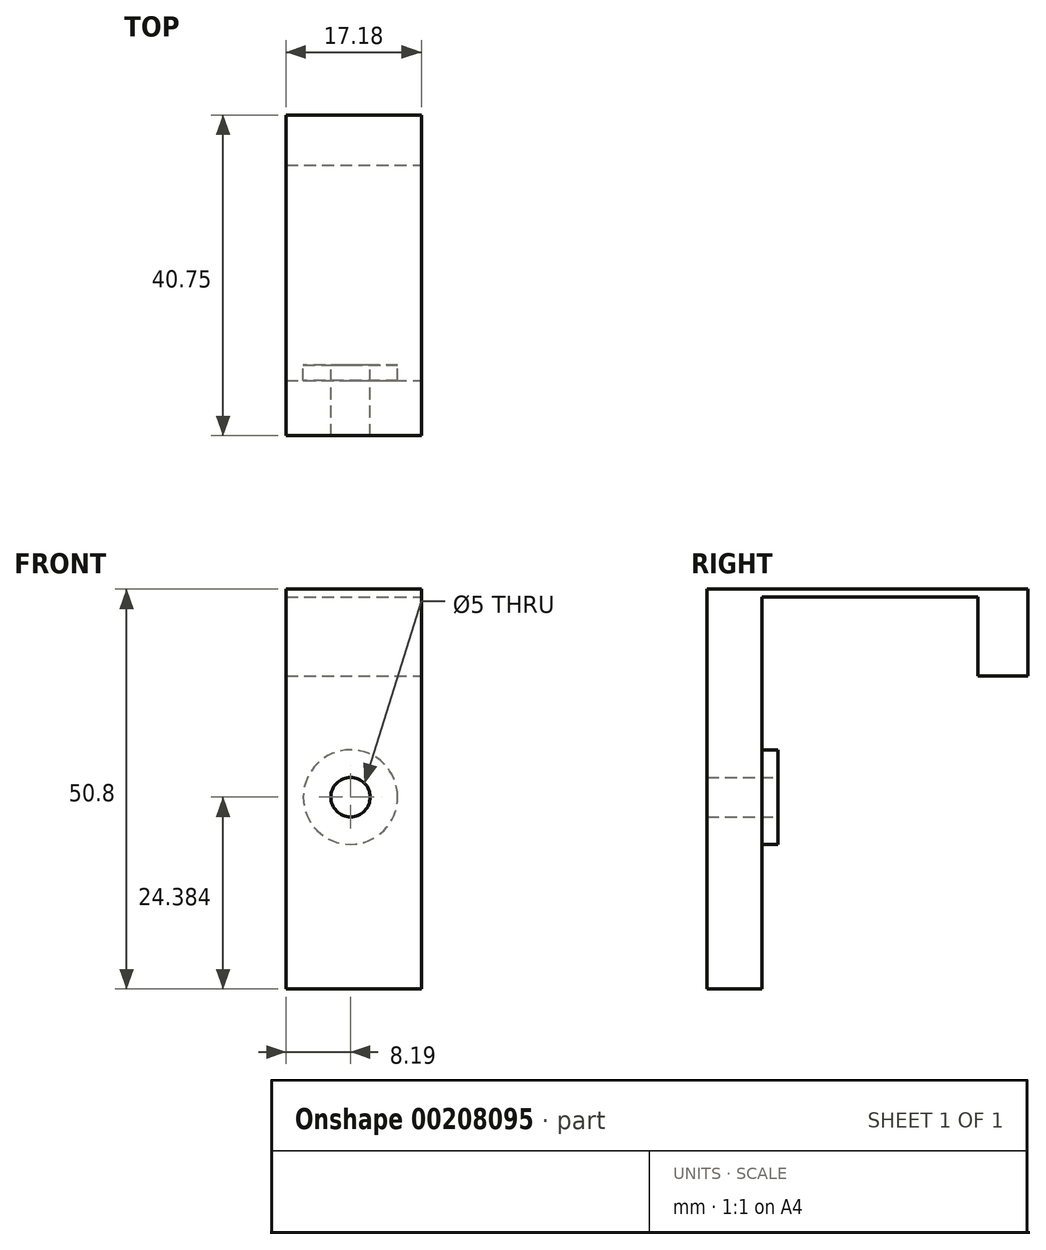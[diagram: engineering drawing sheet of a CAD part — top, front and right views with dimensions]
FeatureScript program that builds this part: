
annotation { "Feature Type Name" : "Feature", "Feature Type Description" : "" }
export const myFeature = defineFeature(function(context is Context, id is Id, definition is map)
    precondition{}
    {
        {
            var Q0;
            Q0=qCreatedBy(makeId("Front.planeOp"),FACE);
            var sketch = newSketch(context, id + "F0", { "sketchPlane" : qUnion([Q0])});
            skLineSegment(sketch, "E0.bottom", {"start": v(25.4, -38.1) * mm, "end": v(-25.4, -38.1) * mm});
            skLineSegment(sketch, "E0.top", {"start": v(25.4, 38.1) * mm, "end": v(-25.4, 38.1) * mm});
            skLineSegment(sketch, "E0.left", {"start": v(25.4, -38.1) * mm, "end": v(25.4, 38.1) * mm});
            skLineSegment(sketch, "E0.right", {"start": v(-25.4, -38.1) * mm, "end": v(-25.4, 38.1) * mm});
            skPoint(sketch, "E0.middle", {"position": v(0, 0) * mm});
            skSolve(sketch);
        }
        {
            var Q0;
            Q0=makeQuery(id+"F0.imprint","IMPRINT",FACE,{"disambiguationData":[TD([[makeQuery(id+"F0.imprint","IMPRINT",EDGE,{"derivedFrom":sQuery(id+"F0.wireOp",EDGE,"E0.bottom")}),-1.0]])]});
            extrude(context, id + "F1", {"entities" : qUnion([Q0]), "depth" : 50.8 * mm});
        }
        {
            var Q0;
            Q0=qCreatedBy(makeId("Front.planeOp"),FACE);
            var sketch = newSketch(context, id + "F2", { "sketchPlane" : qUnion([Q0])});
            skLineSegment(sketch, "E1.bottom", {"start": v(-57.9, 37.08) * mm, "end": v(60.26, 37.08) * mm});
            skLineSegment(sketch, "E1.top", {"start": v(-57.9, -47.42) * mm, "end": v(60.26, -47.42) * mm});
            skLineSegment(sketch, "E1.left", {"start": v(-57.9, 37.08) * mm, "end": v(-57.9, -47.42) * mm});
            skLineSegment(sketch, "E1.right", {"start": v(60.26, 37.08) * mm, "end": v(60.26, -47.42) * mm});
            skLineSegment(sketch, "E2.0", {"start": v(25.4, 37.1) * mm, "end": v(-25.4, 37.1) * mm});
            skSolve(sketch);
        }
        {
            var Q0;
            Q0 = qSketchRegion(id + "F2", true);
            extrude(context, id + "F3", {"entities" : qUnion([Q0]), "depth" : 25.4 * mm});
        }
        {
            var Q0;
            Q0=makeQuery(id+"F3.opExtrude","SWEPT_BODY",BODY,{"disambiguationData":[OSD([sQuery(id+"F2.wireOp",EDGE,"E1.bottom"),sQuery(id+"F2.wireOp",EDGE,"E1.top"),sQuery(id+"F2.wireOp",EDGE,"E1.left"),sQuery(id+"F2.wireOp",EDGE,"E1.right")])]});
            var Q1;
            Q1=qCreatedBy(makeId("Front.planeOp"),FACE);
            transform(context, id + "F4", {"entities" : qUnion([Q0]), "transformType" : TransformType.TRANSLATION_DISTANCE, "transformDirection" : qUnion([Q1]), "distance" : 6.35 * mm, "makeCopy" : false});
        }
        {
            var Q0;
            Q0=makeQuery(id+"F3.opExtrude","SWEPT_BODY",BODY,{"disambiguationData":[OSD([sQuery(id+"F2.wireOp",EDGE,"E1.bottom"),sQuery(id+"F2.wireOp",EDGE,"E1.top"),sQuery(id+"F2.wireOp",EDGE,"E1.left"),sQuery(id+"F2.wireOp",EDGE,"E1.right")])]});
            var Q1;
            Q1=makeQuery(id+"F1.opExtrude","SWEPT_BODY",BODY,{"disambiguationData":[OSD([sQuery(id+"F0.wireOp",EDGE,"E0.bottom"),sQuery(id+"F0.wireOp",EDGE,"E0.top"),sQuery(id+"F0.wireOp",EDGE,"E0.left"),sQuery(id+"F0.wireOp",EDGE,"E0.right")])]});
            booleanBodies(context, id + "F5", {"operationType" : BooleanOperationType.SUBTRACTION, "tools" : qUnion([Q0]), "targets" : qUnion([Q1])});
        }
        {
            var Q0;
            Q0=makeQuery(id+"F5.opBoolean","COPY",FACE,{"derivedFrom":makeQuery(id+"F3.opExtrude","CAP_FACE",FACE,{"disambiguationData":[OSD([sQuery(id+"F2.wireOp",EDGE,"E1.bottom"),sQuery(id+"F2.wireOp",EDGE,"E1.top"),sQuery(id+"F2.wireOp",EDGE,"E1.left"),sQuery(id+"F2.wireOp",EDGE,"E1.right")])],"isStart":false})});
            var sketch = newSketch(context, id + "F6", { "sketchPlane" : qUnion([Q0])});
            skSolve(sketch);
        }
        {
            var Q0;
            Q0=makeQuery(id+"F1.opExtrude","CAP_FACE",FACE,{"disambiguationData":[OSD([sQuery(id+"F0.wireOp",EDGE,"E0.bottom"),sQuery(id+"F0.wireOp",EDGE,"E0.top"),sQuery(id+"F0.wireOp",EDGE,"E0.left"),sQuery(id+"F0.wireOp",EDGE,"E0.right")])],"isStart":true});
            var sketch = newSketch(context, id + "F7", { "sketchPlane" : qUnion([Q0])});
            skLineSegment(sketch, "E3.0", {"start": v(-25.4, 27.1) * mm, "end": v(25.4, 27.1) * mm});
            skSolve(sketch);
        }
        {
            var Q0;
            {var subQ0=sQuery(id+"F7.wireOp",EDGE,"E3.0");Q0=makeQuery(id+"F7.imprint","IMPRINT",FACE,{"disambiguationData":[TD([[makeQuery(id+"F7.imprint","IMPRINT",EDGE,{"derivedFrom":subQ0}),-1.0]])]});}
            extrude(context, id + "F8", {"entities" : qUnion([Q0]), "operationType" : NewBodyOperationType.REMOVE, "oppositeDirection" : true, "depth" : 25.4 * mm});
        }
        {
            var Q0;
            {var subQ0=sQuery(id+"F2.wireOp",EDGE,"E1.bottom");Q0=makeQuery(id+"F6.imprint","IMPRINT",FACE,{"disambiguationData":[TD([[makeQuery(id+"F6.imprint","IMPRINT",EDGE,{"derivedFrom":makeQuery(id+"F5.opBoolean","COPY",EDGE,{"derivedFrom":makeQuery(id+"F3.opExtrude","CAP_EDGE",EDGE,{"disambiguationData":[OSD([subQ0])],"isStart":false})})}),1.0]])]});}
            var sketch = newSketch(context, id + "F9", { "sketchPlane" : qUnion([Q0])});
            skLineSegment(sketch, "E4.0", {"start": v(25.4, 11.68) * mm, "end": v(-25.4, 11.68) * mm});
            skCircle(sketch, "E5", {"center": v(0, 11.68) * mm, "radius": 6 * mm});
            skSolve(sketch);
        }
        {
            var Q0;
            {var subQ0=sQuery(id+"F9.wireOp",EDGE,"E5");var subQ1=sQuery(id+"F9.wireOp",EDGE,"E4.0");var subQ2=makeQuery(id+"F9.imprint","INTERSECT",VERTEX,{"disambiguationData":[OD(0.0)],"derivedFrom":[subQ1,subQ0]});Q0=makeQuery(id+"F9.imprint","IMPRINT",FACE,{"disambiguationData":[TD([[makeQuery(id+"F9.imprint","IMPRINT",EDGE,{"disambiguationData":[TD([[subQ2,-1.0]])],"derivedFrom":subQ1}),-1.0]])]});}
            var Q1;
            {var subQ0=sQuery(id+"F9.wireOp",EDGE,"E5");var subQ1=sQuery(id+"F9.wireOp",EDGE,"E4.0");var subQ2=makeQuery(id+"F9.imprint","INTERSECT",VERTEX,{"disambiguationData":[OD(0.0)],"derivedFrom":[subQ1,subQ0]});Q1=makeQuery(id+"F9.imprint","IMPRINT",FACE,{"disambiguationData":[TD([[makeQuery(id+"F9.imprint","IMPRINT",EDGE,{"disambiguationData":[TD([[subQ2,-1.0]])],"derivedFrom":subQ1}),1.0]])]});}
            extrude(context, id + "F10", {"entities" : qUnion([Q0, Q1]), "operationType" : NewBodyOperationType.REMOVE, "oppositeDirection" : true, "depth" : 2 * mm});
        }
        {
            var Q0;
            {var subQ0=sQuery(id+"F2.wireOp",EDGE,"E1.bottom");Q0=makeQuery(id+"F6.imprint","IMPRINT",FACE,{"disambiguationData":[TD([[makeQuery(id+"F6.imprint","IMPRINT",EDGE,{"derivedFrom":makeQuery(id+"F5.opBoolean","COPY",EDGE,{"derivedFrom":makeQuery(id+"F3.opExtrude","CAP_EDGE",EDGE,{"disambiguationData":[OSD([subQ0])],"isStart":false})})}),1.0]])]});}
            var sketch = newSketch(context, id + "F11", { "sketchPlane" : qUnion([Q0])});
            skCircle(sketch, "E6", {"center": v(0, 11.68) * mm, "radius": 2.5 * mm});
            skSolve(sketch);
        }
        {
            var Q0;
            Q0=makeQuery(id+"F11.imprint","IMPRINT",FACE,{"disambiguationData":[TD([[makeQuery(id+"F11.imprint","IMPRINT",EDGE,{"derivedFrom":sQuery(id+"F11.wireOp",EDGE,"E6")}),1.0]])]});
            extrude(context, id + "F12", {"entities" : qUnion([Q0]), "operationType" : NewBodyOperationType.REMOVE, "oppositeDirection" : true, "depth" : 25.4 * mm});
        }
        {
            var Q0;
            Q0=makeQuery(id+"F1.opExtrude","CAP_FACE",FACE,{"disambiguationData":[OSD([sQuery(id+"F0.wireOp",EDGE,"E0.bottom"),sQuery(id+"F0.wireOp",EDGE,"E0.top"),sQuery(id+"F0.wireOp",EDGE,"E0.left"),sQuery(id+"F0.wireOp",EDGE,"E0.right")])],"isStart":false});
            var sketch = newSketch(context, id + "F13", { "sketchPlane" : qUnion([Q0])});
            skLineSegment(sketch, "E7.0", {"start": v(25.4, -12.7) * mm, "end": v(-25.4, -12.7) * mm});
            skSolve(sketch);
        }
        {
            var Q0;
            {var subQ0=sQuery(id+"F13.wireOp",EDGE,"E7.0");Q0=makeQuery(id+"F13.imprint","IMPRINT",FACE,{"disambiguationData":[TD([[makeQuery(id+"F13.imprint","IMPRINT",EDGE,{"derivedFrom":subQ0}),1.0]])]});}
            extrude(context, id + "F14", {"entities" : qUnion([Q0]), "operationType" : NewBodyOperationType.REMOVE, "oppositeDirection" : true, "depth" : 25.4 * mm});
        }
        {
            var Q0;
            Q0=qCreatedBy(makeId("Front.planeOp"),FACE);
            var sketch = newSketch(context, id + "F15", { "sketchPlane" : qUnion([Q0])});
            skLineSegment(sketch, "E8.bottom", {"start": v(9, 38.4) * mm, "end": v(32.67, 38.4) * mm});
            skLineSegment(sketch, "E8.top", {"start": v(9, -15) * mm, "end": v(32.67, -15) * mm});
            skLineSegment(sketch, "E8.left", {"start": v(9, 38.4) * mm, "end": v(9, -15) * mm});
            skLineSegment(sketch, "E8.right", {"start": v(32.67, 38.4) * mm, "end": v(32.67, -15) * mm});
            skLineSegment(sketch, "E9.bottom", {"start": v(28.87, 38.4) * mm, "end": v(32.67, 38.4) * mm});
            skLineSegment(sketch, "E9.top", {"start": v(28.87, 38.4) * mm, "end": v(32.67, 38.4) * mm});
            skLineSegment(sketch, "E9.left", {"start": v(28.87, 38.4) * mm, "end": v(28.87, 38.4) * mm});
            skLineSegment(sketch, "E9.right", {"start": v(32.67, 38.4) * mm, "end": v(32.67, 38.4) * mm});
            skSolve(sketch);
        }
        {
            var Q0;
            Q0=makeQuery(id+"F15.imprint","IMPRINT",FACE,{"disambiguationData":[TD([[makeQuery(id+"F15.imprint","IMPRINT",EDGE,{"derivedFrom":sQuery(id+"F15.wireOp",EDGE,"E8.bottom")}),-1.0]])]});
            extrude(context, id + "F16", {"entities" : qUnion([Q0]), "operationType" : NewBodyOperationType.REMOVE, "depth" : 76.2 * mm});
        }
        {
            var Q0;
            Q0=qCreatedBy(makeId("Front.planeOp"),FACE);
            var sketch = newSketch(context, id + "F17", { "sketchPlane" : qUnion([Q0])});
            skLineSegment(sketch, "E10.bottom", {"start": v(-8.19, -16.3) * mm, "end": v(-28.8, -16.3) * mm});
            skLineSegment(sketch, "E10.top", {"start": v(-8.19, 43.29) * mm, "end": v(-28.8, 43.29) * mm});
            skLineSegment(sketch, "E10.left", {"start": v(-8.19, -16.3) * mm, "end": v(-8.19, 43.29) * mm});
            skLineSegment(sketch, "E10.right", {"start": v(-28.8, -16.3) * mm, "end": v(-28.8, 43.29) * mm});
            skSolve(sketch);
        }
        {
            var Q0;
            Q0=makeQuery(id+"F17.imprint","IMPRINT",FACE,{"disambiguationData":[TD([[makeQuery(id+"F17.imprint","IMPRINT",EDGE,{"derivedFrom":sQuery(id+"F17.wireOp",EDGE,"E10.bottom")}),-1.0]])]});
            extrude(context, id + "F18", {"entities" : qUnion([Q0]), "operationType" : NewBodyOperationType.REMOVE, "depth" : 50.8 * mm});
        }
        {
            var Q0;
            Q0=qCreatedBy(makeId("Right.planeOp"),FACE);
            var sketch = newSketch(context, id + "F19", { "sketchPlane" : qUnion([Q0])});
            skLineSegment(sketch, "E11.bottom", {"start": v(-40.75, 39.06) * mm, "end": v(-55.86, 39.06) * mm});
            skLineSegment(sketch, "E11.top", {"start": v(-40.75, -15) * mm, "end": v(-55.86, -15) * mm});
            skLineSegment(sketch, "E11.left", {"start": v(-40.75, 39.06) * mm, "end": v(-40.75, -15) * mm});
            skLineSegment(sketch, "E11.right", {"start": v(-55.86, 39.06) * mm, "end": v(-55.86, -15) * mm});
            skSolve(sketch);
        }
        {
            var Q0;
            Q0 = qSketchRegion(id + "F19", true);
            extrude(context, id + "F20", {"entities" : qUnion([Q0]), "operationType" : NewBodyOperationType.REMOVE, "oppositeDirection" : true, "depth" : 12.7 * mm});
        }
        {
            var Q0;
            Q0=makeQuery(id+"F19.imprint","IMPRINT",FACE,{"disambiguationData":[TD([[makeQuery(id+"F19.imprint","IMPRINT",EDGE,{"derivedFrom":sQuery(id+"F19.wireOp",EDGE,"E11.bottom")}),1.0]])]});
            extrude(context, id + "F21", {"entities" : qUnion([Q0]), "operationType" : NewBodyOperationType.REMOVE, "depth" : 12.7 * mm});
        }
    });
